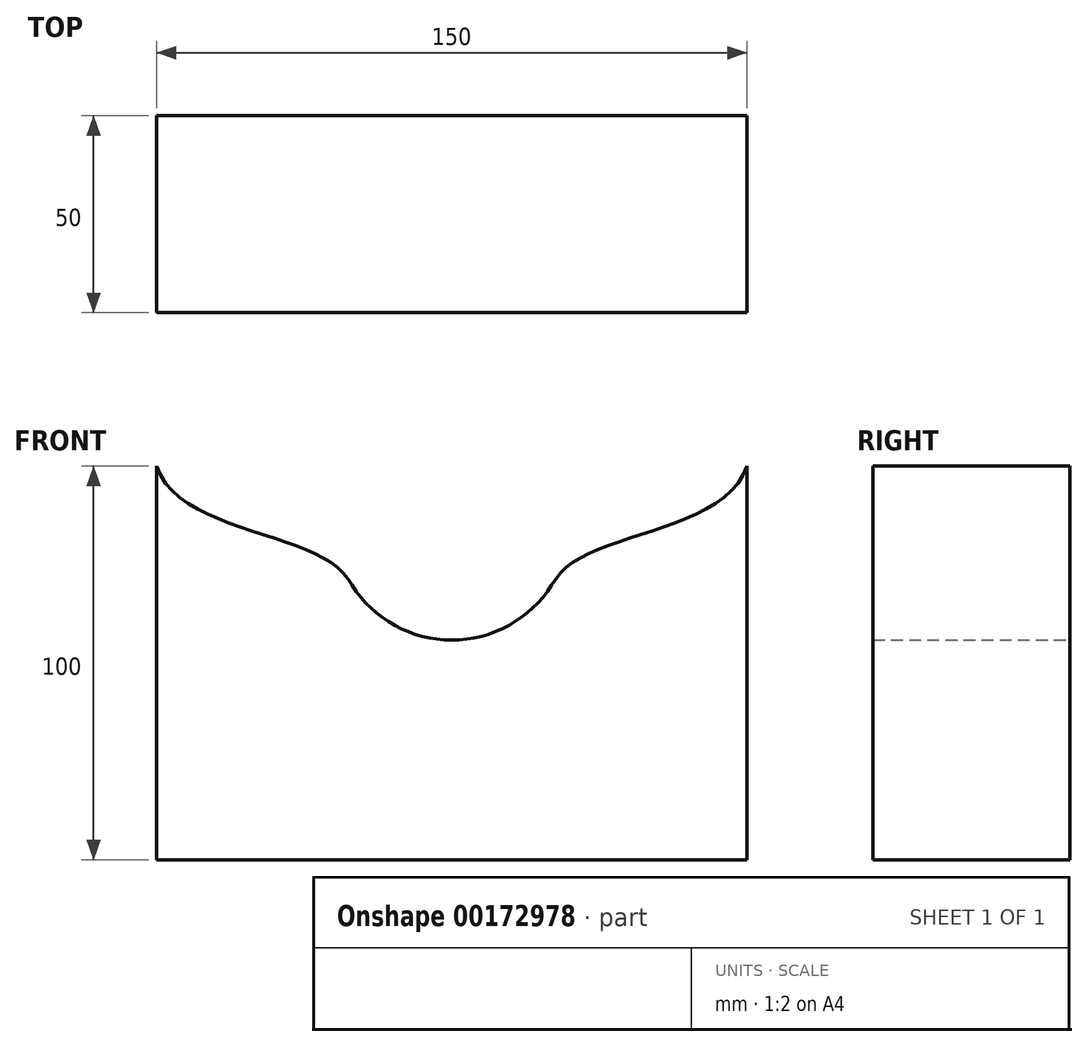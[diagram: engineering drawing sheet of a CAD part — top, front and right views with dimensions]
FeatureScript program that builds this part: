
annotation { "Feature Type Name" : "Feature", "Feature Type Description" : "" }
export const myFeature = defineFeature(function(context is Context, id is Id, definition is map)
    precondition{}
    {
        {
            var Q0;
            Q0=qCreatedBy(makeId("Front.planeOp"),FACE);
            var sketch = newSketch(context, id + "F0", { "sketchPlane" : qUnion([Q0])});
            skLineSegment(sketch, "E0", {"start": v(0, -50) * mm, "end": v(-75, -50) * mm});
            skLineSegment(sketch, "E1", {"start": v(-75, -50) * mm, "end": v(-75, 50) * mm});
            skFitSpline(sketch, "E2", {"points": [v(-75, 50) * mm, v(-30, 25) * mm, v(0, 0) * mm], "startDerivative": vector(29.12, -86.85) * mm, "endDerivative": vector(158.12, -32.95) * mm});
            skLineSegment(sketch, "E3", {"start": v(0, 0) * mm, "end": v(0, -50) * mm, "construction": true});
            skFitSpline(sketch, "E4.MirrorCS", {"points": [v(75, 50) * mm, v(30, 25) * mm, v(0, 0) * mm], "startDerivative": vector(-29.12, -86.85) * mm, "endDerivative": vector(-158.12, -32.95) * mm});
            skLineSegment(sketch, "E5.MirrorCS", {"start": v(75, -50) * mm, "end": v(75, 50) * mm});
            skLineSegment(sketch, "E6.MirrorCS", {"start": v(0, -50) * mm, "end": v(75, -50) * mm});
            skSolve(sketch);
        }
        {
            var Q0;
            Q0 = qSketchRegion(id + "F0", true);
            extrude(context, id + "F1", {"entities" : qUnion([Q0]), "depth" : 50 * mm});
        }
        {
            var Q0;
            Q0=makeQuery(id+"F1.opExtrude","SWEPT_EDGE",EDGE,{"disambiguationData":[OSD([sQuery(id+"F0.wireOp",EDGE,"E2"),sQuery(id+"F0.wireOp",EDGE,"E4.MirrorCS")])]});
            fillet(context, id + "F2", {"entities" : qUnion([Q0]), "radius" : 30 * mm, "tangentPropagation" : true, "allowEdgeOverflow" : false});
        }
    });
